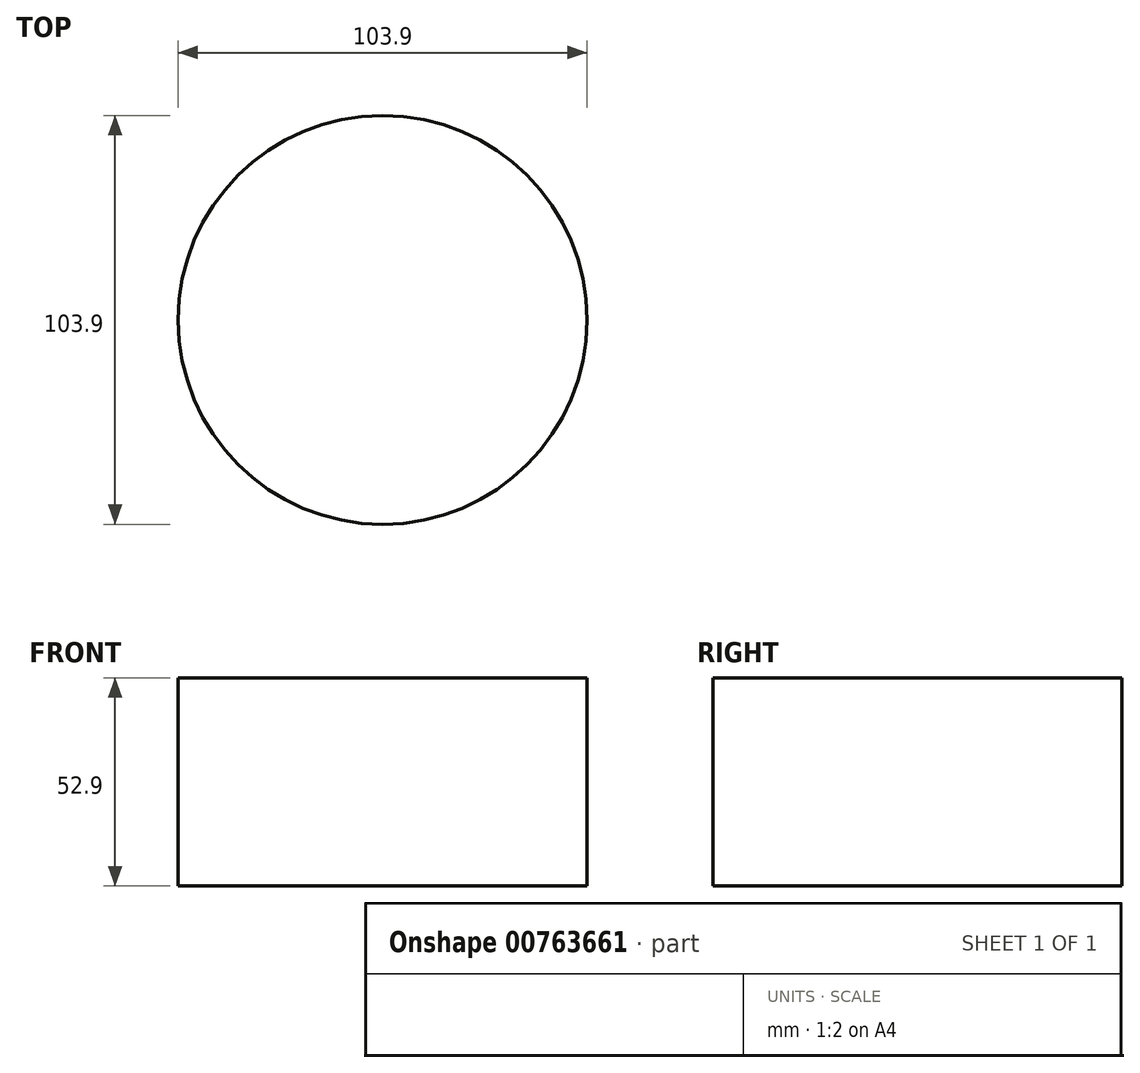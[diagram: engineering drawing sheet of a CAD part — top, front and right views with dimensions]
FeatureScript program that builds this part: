
annotation { "Feature Type Name" : "Feature", "Feature Type Description" : "" }
export const myFeature = defineFeature(function(context is Context, id is Id, definition is map)
    precondition{}
    {
        {
            var Q0;
            Q0=qCreatedBy(makeId("Front.planeOp"),FACE);
            var sketch = newSketch(context, id + "F0", { "sketchPlane" : qUnion([Q0])});
            skLineSegment(sketch, "E0.bottom", {"start": v(-25.88, 26.26) * mm, "end": v(26.07, 26.26) * mm});
            skLineSegment(sketch, "E0.top", {"start": v(-25.88, -26.64) * mm, "end": v(26.07, -26.64) * mm});
            skLineSegment(sketch, "E0.left", {"start": v(-25.88, 26.26) * mm, "end": v(-25.88, -26.64) * mm});
            skLineSegment(sketch, "E0.right", {"start": v(26.07, 26.26) * mm, "end": v(26.07, -26.64) * mm});
            skSolve(sketch);
        }
        {
            var Q0;
            Q0=makeQuery(id+"F0.imprint","IMPRINT",FACE,{"disambiguationData":[TD([[makeQuery(id+"F0.imprint","IMPRINT",EDGE,{"derivedFrom":sQuery(id+"F0.wireOp",EDGE,"E0.bottom")}),-1.0]])]});
            var Q1;
            Q1=sQuery(id+"F0.wireOp",EDGE,"E0.left");
            revolve(context, id + "F1", {"surfaceOperationType" : NewSurfaceOperationType.NEW, "entities" : qUnion([Q0]), "axis" : qUnion([Q1]), "revolveType" : RevolveType.FULL});
        }
    });
